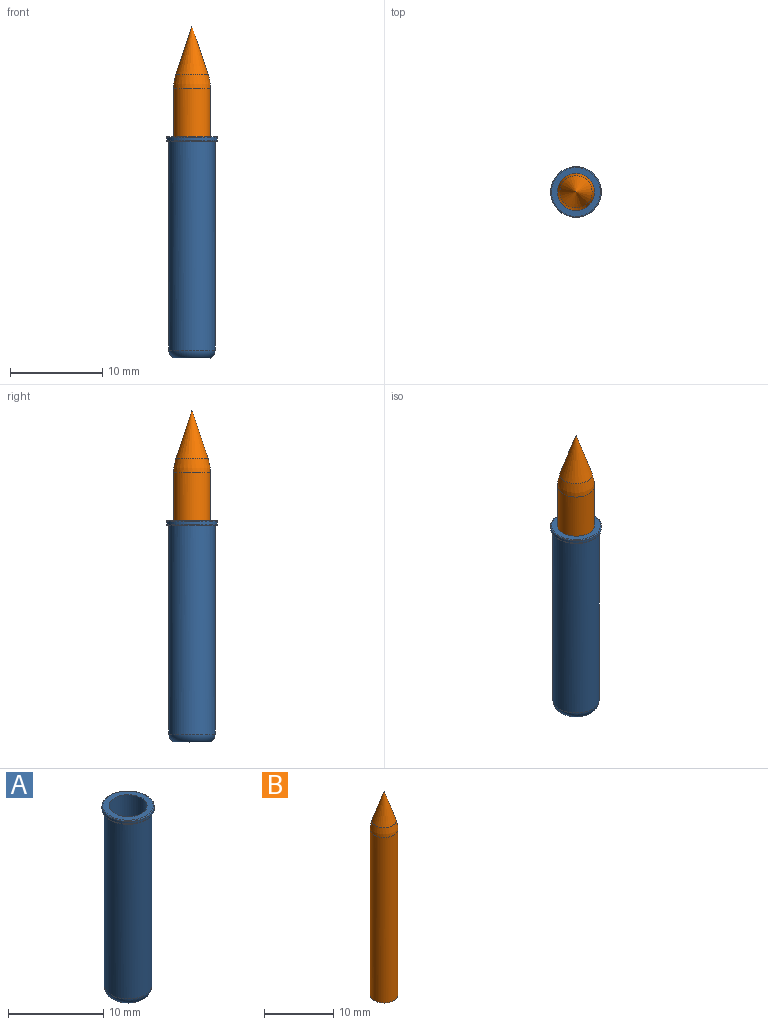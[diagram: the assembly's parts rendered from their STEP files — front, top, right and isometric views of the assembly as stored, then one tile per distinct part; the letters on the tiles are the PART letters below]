
ASSEMBLY  parts=2 mates=1
PART A: 8 faces, bbox 6x6x24.1 mm
  f0: cylinder r=2mm len=24mm, axis (0,0,1), area 301.6mm2, adj f3,f5
  f1: cylinder r=2.75mm len=5.5mm, axis (0,0,1), area 5.2mm2, adj f6,f7
  f2: plane 5.3x5.3mm, normal (0,0,-1), area 2.4mm2, adj f4,f7
  f3: plane 5.3x5.3mm, normal (0,0,1), area 9.5mm2, adj f0,f6
  f4: cylinder r=2.5mm len=22.63mm, axis (0,0,1), area 355.5mm2, adj f2,f5
  f5: torus R=1.5mm, axis (0,0,-1), area 15.3mm2, adj f0,f4
  f6: torus R=2.65mm, axis (0,0,1), area 2.7mm2, adj f1,f3
  f7: torus R=2.65mm, axis (0,0,1), area 2.7mm2, adj f1,f2
PART B: 4 faces, bbox 4x4x36 mm
  f0: cylinder r=2mm len=29.19mm, axis (0,0,1), area 366.8mm2, adj f2,f3
  f1: cone r=2mm half-angle=18.4deg, axis (0,0,-1), area 30.2mm2, adj f2
  f2: revolved ~4x4mm, area 19.3mm2, adj f0,f1
  f3: plane 4x4mm, normal (0,0,-1), area 12.6mm2, adj f0
PLACE A t=(-0.94,0.09,0.87)mm fixed
PLACE B t=(-0.94,0.09,0.87)mm
MATE slider B.f0 <-> A.f0  axis (0,0,-1) through (-0.94,0.09,-23.13)mm
